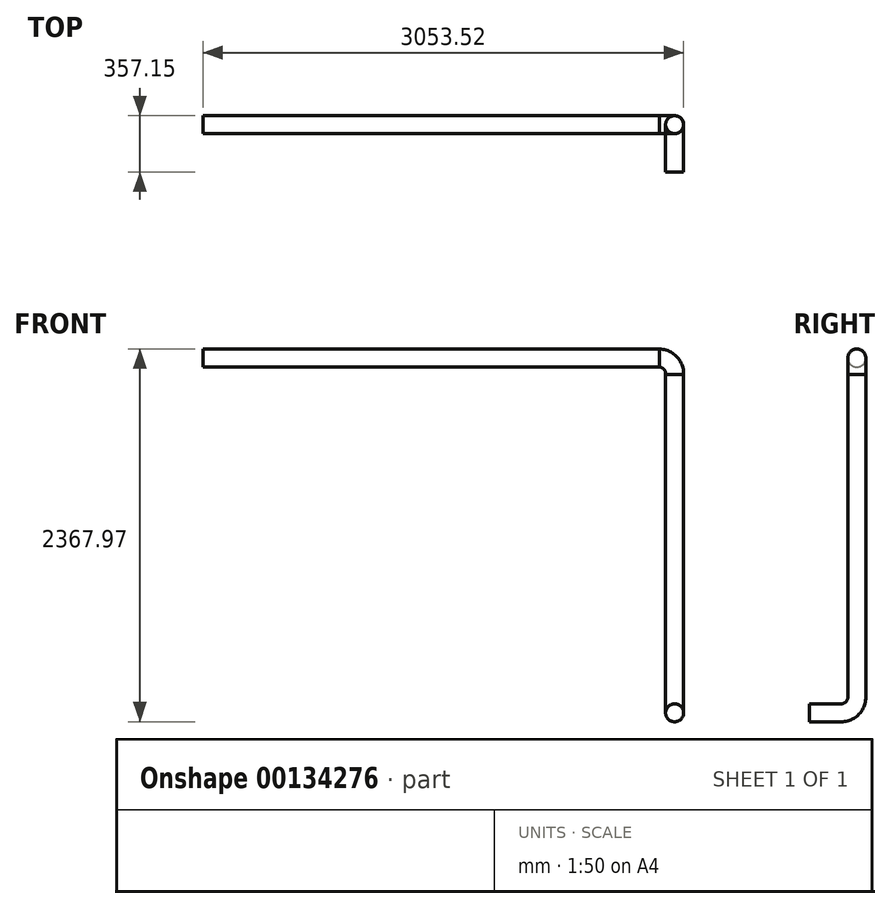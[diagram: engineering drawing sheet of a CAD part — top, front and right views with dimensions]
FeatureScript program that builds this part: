
annotation { "Feature Type Name" : "Feature", "Feature Type Description" : "" }
export const myFeature = defineFeature(function(context is Context, id is Id, definition is map)
    precondition{}
    {
        {
            var Q0;
            Q0=qCreatedBy(makeId("Front.planeOp"),FACE);
            cPlane(context, id + "F0", {"entities" : qUnion([Q0]), "cplaneType" : CPlaneType.OFFSET, "offset" : 300 * mm, "oppositeDirection" : true, "width" : 150 * mm, "height" : 150 * mm});
        }
        {
            var Q0;
            Q0=qCreatedBy(makeId("Right.planeOp"),FACE);
            var sketch = newSketch(context, id + "F1", { "sketchPlane" : qUnion([Q0])});
            skLineSegment(sketch, "E0", {"start": v(0, 0) * mm, "end": v(200, 0) * mm});
            skLineSegment(sketch, "E1", {"start": v(300, 100) * mm, "end": v(300, 2000) * mm});
            skPoint(sketch, "E2.visualSharp", {"position": v(300, 0) * mm});
            skArc(sketch, "E2.filletArc", {"start": v(200, 0) * mm, "mid": v(270.71, 29.29) * mm, "end": v(300, 100) * mm});
            skSolve(sketch);
        }
        {
            var Q0;
            Q0=qCreatedBy(makeId("Front.planeOp"),FACE);
            var sketch = newSketch(context, id + "F2", { "sketchPlane" : qUnion([Q0])});
            skCircle(sketch, "E3", {"center": v(0, 0) * mm, "radius": 57.15 * mm});
            skSolve(sketch);
        }
        {
            var Q0;
            Q0=makeQuery(id+"F2.imprint","IMPRINT",FACE,{"disambiguationData":[TD([[makeQuery(id+"F2.imprint","IMPRINT",EDGE,{"derivedFrom":sQuery(id+"F2.wireOp",EDGE,"E3")}),1.0]])]});
            var Q1;
            Q1=sQuery(id+"F1.wireOp",EDGE,"E0");
            var Q2;
            Q2=sQuery(id+"F1.wireOp",EDGE,"E2.filletArc");
            var Q3;
            Q3=sQuery(id+"F1.wireOp",EDGE,"E1");
            sweep(context, id + "F3", {"profiles" : qUnion([Q0]), "path" : qUnion([Q1, Q2, Q3])});
        }
        {
            var Q0;
            Q0=makeQuery(id+"F3.opSweep","CAP_FACE",FACE,{"disambiguationData":[OSD([sQuery(id+"F1.wireOp",VERTEX,"E1.end"),sQuery(id+"F2.wireOp",EDGE,"E3")])],"isStart":false});
            var sketch = newSketch(context, id + "F4", { "sketchPlane" : qUnion([Q0])});
            skCircle(sketch, "E4.0", {"center": v(0, 300) * mm, "radius": 57.15 * mm});
            skSolve(sketch);
        }
        {
            var Q0;
            Q0=qCreatedBy(id+"F0.planeOp",FACE);
            var sketch = newSketch(context, id + "F5", { "sketchPlane" : qUnion([Q0])});
            skLineSegment(sketch, "E5", {"start": v(0, 2003.67) * mm, "end": v(0, 2153.67) * mm});
            skLineSegment(sketch, "E6", {"start": v(-100, 2253.67) * mm, "end": v(-3000, 2253.67) * mm});
            skPoint(sketch, "E7.visualSharp", {"position": v(0, 2253.67) * mm});
            skArc(sketch, "E7.filletArc", {"start": v(0, 2153.67) * mm, "mid": v(-29.29, 2224.38) * mm, "end": v(-100, 2253.67) * mm});
            skSolve(sketch);
        }
        {
            var Q0;
            Q0 = qSketchRegion(id + "F4", true);
            var Q1;
            Q1 = qConstructionFilter(qBodyType(qCreatedBy(id + "F5" ,EDGE), BodyType.WIRE), ConstructionObject.NO);
            sweep(context, id + "F6", {"operationType" : NewBodyOperationType.ADD, "profiles" : qUnion([Q0]), "path" : qUnion([Q1])});
        }
    });
